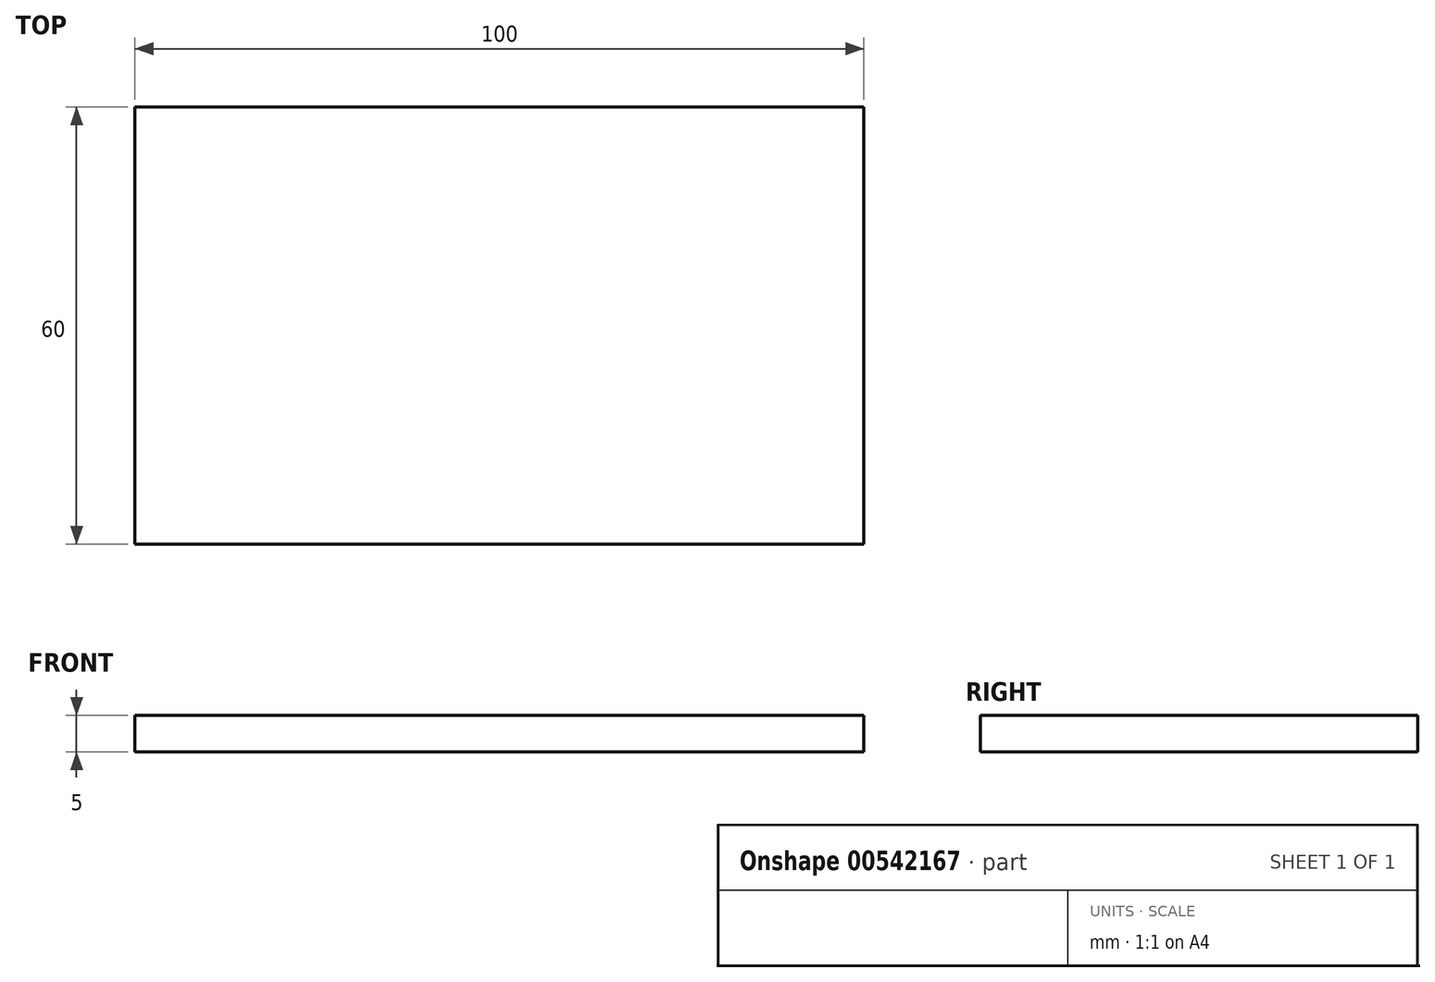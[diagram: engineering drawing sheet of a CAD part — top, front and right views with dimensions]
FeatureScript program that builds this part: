
annotation { "Feature Type Name" : "Feature", "Feature Type Description" : "" }
export const myFeature = defineFeature(function(context is Context, id is Id, definition is map)
    precondition{}
    {
        {
            var Q0;
            Q0=qCreatedBy(makeId("Top.planeOp"),FACE);
            var sketch = newSketch(context, id + "F0", { "sketchPlane" : qUnion([Q0])});
            skLineSegment(sketch, "E0.bottom", {"start": v(-50, 30) * mm, "end": v(50, 30) * mm});
            skLineSegment(sketch, "E0.top", {"start": v(-50, -30) * mm, "end": v(50, -30) * mm});
            skLineSegment(sketch, "E0.left", {"start": v(-50, 30) * mm, "end": v(-50, -30) * mm});
            skLineSegment(sketch, "E0.right", {"start": v(50, 30) * mm, "end": v(50, -30) * mm});
            skLineSegment(sketch, "E1", {"start": v(-50, 30) * mm, "end": v(50, -30) * mm, "construction": true});
            skPoint(sketch, "E2", {"position": v(0, 0) * mm});
            skSolve(sketch);
        }
        {
            var Q0;
            Q0=makeQuery(id+"F0.imprint","IMPRINT",FACE,{"disambiguationData":[TD([[makeQuery(id+"F0.imprint","IMPRINT",EDGE,{"derivedFrom":sQuery(id+"F0.wireOp",EDGE,"E0.bottom")}),-1.0]])]});
            extrude(context, id + "F1", {"entities" : qUnion([Q0]), "depth" : 5 * mm, "offsetDistance" : 25 * mm});
        }
    });
